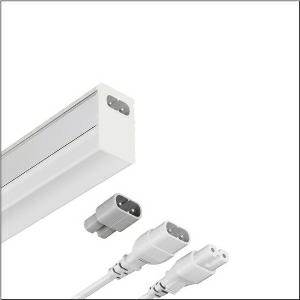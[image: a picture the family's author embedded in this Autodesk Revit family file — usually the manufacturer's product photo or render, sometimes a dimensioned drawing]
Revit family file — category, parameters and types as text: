
# Revit family: siluette_r__41-e_51lp327km20ae_d0b8
name_source: partatom
category: Lighting Fixtures
units: mm (PartAtom-declared; Revit-internal decimal feet)

## family parameters
Cut with Voids When Loaded = No
Host = Face
Light Source = No
Part Type = Normal
Room Calculation Point = No
Round Connector Dimension = Use Diameter
Shared = No

## types (1)
- --- (1 x LED, 2000 lm, 16 W, 5000K)
    Apparent Load = 16 VA
    CIE Flux Codes = 37 66 87 87 100
    Color Rendering = 80
    Color Temperature = 5000K
    Default Elevation = 1800 mm
    Description = Siluette® 41-E, batten luminaire, primary optical cover: cover, of PC, frosted, light emission: direct distribution, primary light characteristic: symmetric, installation type: surface-mounted, LED, rated luminous flux: 2.000lm, luminous efficacy: 125lm/W, light colour: 830/840/850, colour temperature: 3000/4000/5000K, control gear: ON/OFF, with system connector: socket, mains connection: 220..240V, AC, 50/60Hz, rated input power: 16W, housing, of aluminium, silver, length: 1.180mm, width: 25mm, height: 44mm, end cap, of PC, white, protection rating (complete): IP20, insulation class (complete): insulation class II (safety insulation), certification: CE, permissible operating ambient temperature: -20..+40°C, packaging unit: 1 piece
    Height = 44 mm
    Lamp = 1 x LED
    Lamp Light Flux = 2000 lm
    Lamp Power = 16 W
    Lamp count = 1
    Length = 1180 mm
    Luminous efficacy = 125 lm/W
    Manufacturer = Siteco
    ModVariant = No
    Model = 51LP327KM20AE
    Mounting Place = Ceiling
    Mounting Type = Surface mounted
    Number of Poles = 1
    OnlyDefault = Yes
    Power Factor = 1
    Product Name = Siluette® 41-E
    Product group = batten luminaire
    ProductGroupID = 304
    Protection Class = Protection class II
    Protection Degree = IP 20
    RLX_Detail_Level = 1
    RLX_Emergency_Light_Flux = 0 lm
    RLX_Emergency_Type = 0
    RLX_Emergency_Type_DB = No
    RlxData = <blob elided: 37425 chars, md5=d888841b>
    Socket = socket
    Standby Power = 0 W
    System Light Flux = 2000 lm
    System Power = 16 W
    Type Comments = individual setting: colour temperature 5000K
    Type Image = l_1007257.jpg
    URL = http://relux.com
    VarID = @adj_042781
    Voltage = 0 V
    Weight = 0.00 kg
    Width = 25 mm  [stored 0.082021 ft]

note: [stored X ft] marks values corroborated as IEEE doubles in the binary element streams (Revit-internal decimal feet)

## geometry (parser evidence)
native form markers: Blend x4, Sweep x13
no freeform markers — native parametric forms only
